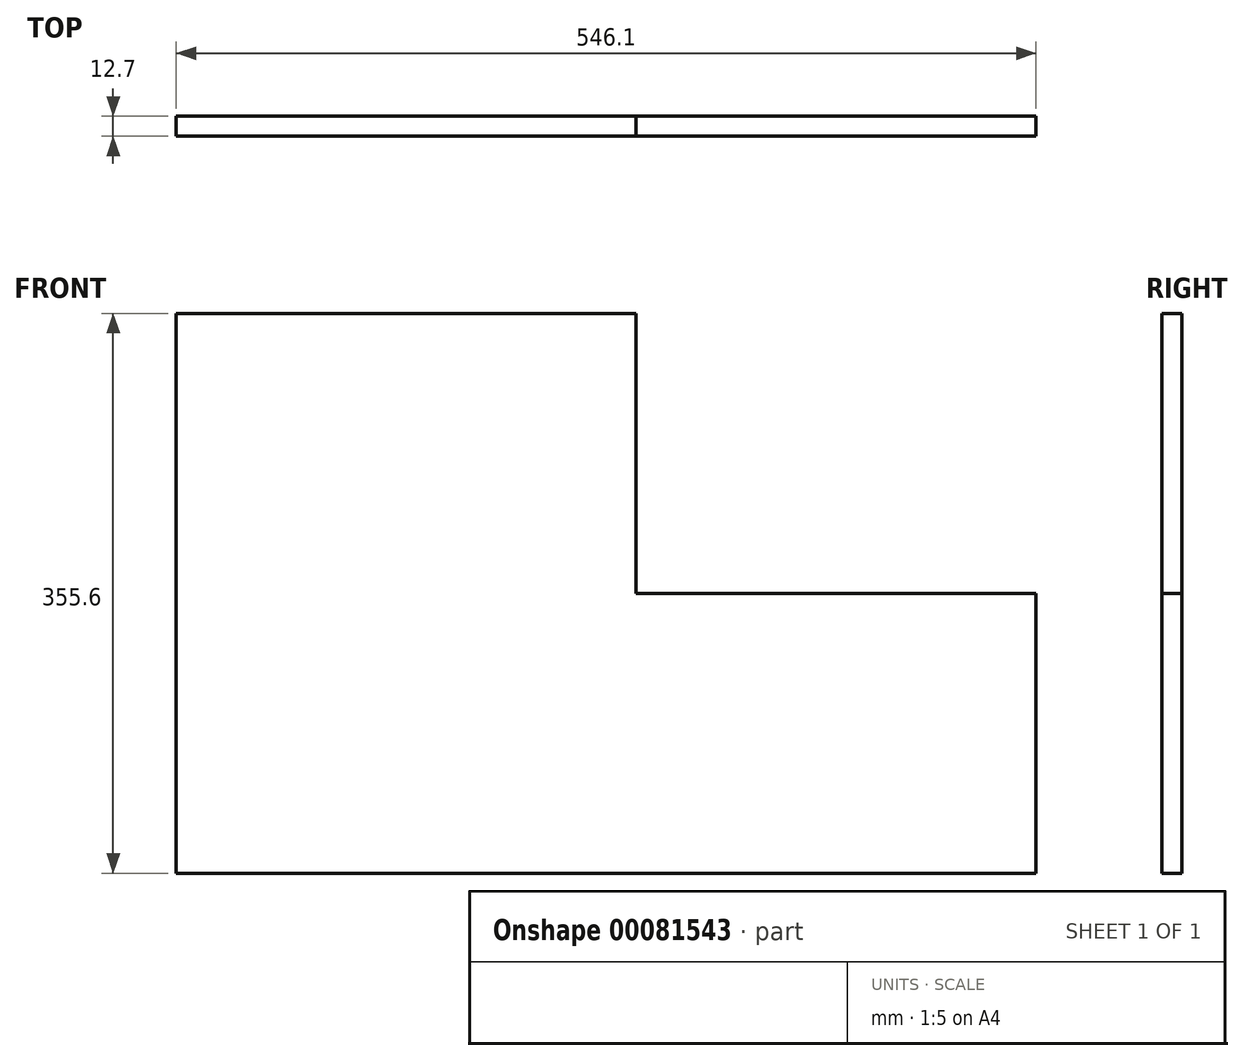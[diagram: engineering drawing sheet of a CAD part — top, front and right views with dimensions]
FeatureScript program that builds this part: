
annotation { "Feature Type Name" : "Feature", "Feature Type Description" : "" }
export const myFeature = defineFeature(function(context is Context, id is Id, definition is map)
    precondition{}
    {
        {
            var Q0;
            Q0=qCreatedBy(makeId("Front.planeOp"),FACE);
            var sketch = newSketch(context, id + "F0", { "sketchPlane" : qUnion([Q0])});
            skLineSegment(sketch, "E0.bottom", {"start": v(273.05, 171.85) * mm, "end": v(-273.05, 171.85) * mm});
            skLineSegment(sketch, "E0.top", {"start": v(273.05, -183.75) * mm, "end": v(-273.05, -183.75) * mm});
            skLineSegment(sketch, "E0.left", {"start": v(273.05, 171.85) * mm, "end": v(273.05, -183.75) * mm});
            skLineSegment(sketch, "E0.right", {"start": v(-273.05, 171.85) * mm, "end": v(-273.05, -183.75) * mm});
            skPoint(sketch, "E0.middle", {"position": v(0, -5.95) * mm});
            skSolve(sketch);
        }
        {
            var Q0;
            Q0 = qSketchRegion(id + "F0", true);
            extrude(context, id + "F1", {"entities" : qUnion([Q0]), "depth" : 12.7 * mm});
        }
        {
            var Q0;
            Q0=makeQuery(id+"F1.opExtrude","CAP_FACE",FACE,{"disambiguationData":[OSD([sQuery(id+"F0.wireOp",EDGE,"E0.bottom"),sQuery(id+"F0.wireOp",EDGE,"E0.top"),sQuery(id+"F0.wireOp",EDGE,"E0.left"),sQuery(id+"F0.wireOp",EDGE,"E0.right")])],"isStart":false});
            var sketch = newSketch(context, id + "F2", { "sketchPlane" : qUnion([Q0])});
            skLineSegment(sketch, "E1.bottom", {"start": v(273.05, 171.85) * mm, "end": v(19.05, 171.85) * mm});
            skLineSegment(sketch, "E1.top", {"start": v(273.05, -5.95) * mm, "end": v(19.05, -5.95) * mm});
            skLineSegment(sketch, "E1.left", {"start": v(273.05, 171.85) * mm, "end": v(273.05, -5.95) * mm});
            skLineSegment(sketch, "E1.right", {"start": v(19.05, 171.85) * mm, "end": v(19.05, -5.95) * mm});
            skSolve(sketch);
        }
        {
            var Q0;
            Q0 = qSketchRegion(id + "F2", true);
            extrude(context, id + "F3", {"entities" : qUnion([Q0]), "operationType" : NewBodyOperationType.REMOVE, "endBound" : BoundingType.THROUGH_ALL, "oppositeDirection" : true, "depth" : 25.4 * mm});
        }
    });
